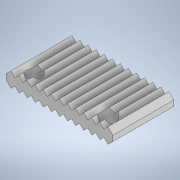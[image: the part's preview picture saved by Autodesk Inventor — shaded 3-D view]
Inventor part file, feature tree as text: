
AUTODESK INVENTOR PART (.ipt)
format: ipt  version: 2020 (Build 240168000, 168)  size: 210,432 bytes
history: native  units: in
note: dims shown in document units (in); Inventor stores cm internally (conversion verified against a paired STEP export)
features: extrude x3, sketch x3, mirror x1
ambient origin geometry x8: Origin, YZ Plane, XZ Plane, XY Plane, X Axis, Y Axis, Z Axis, Center Point
bodies: Solid1 (feature_tree)
feature tree (7):
  extrude  "Extrusion1"  Depth=0.6299in
  extrude  "Extrusion2"  Depth=0.5512in
  mirror  "Mirror1"
  extrude  "Extrusion3"  TaperAngle=135.0deg  [1 undecoded]
  sketch  "Sketch1"  dims[d0=1.1024in d1=0.6299in]
  sketch  "Sketch2"  dims[d2=0.1575in d3=0.0in d4=0.5512in]
  sketch  "Sketch3"  dims[d5=0.0591in d6=135.0deg d7=0.0591in d8=1.9685in d9=0.0in d10=0.1575in d11=0.1575in d12=1.9685in d13=0.0in]
note: 1 required parameter value undecoded (feature->parameter linkage not recoverable at this tier; creation-order binding heuristic only, values carry confidence <= 0.55)
